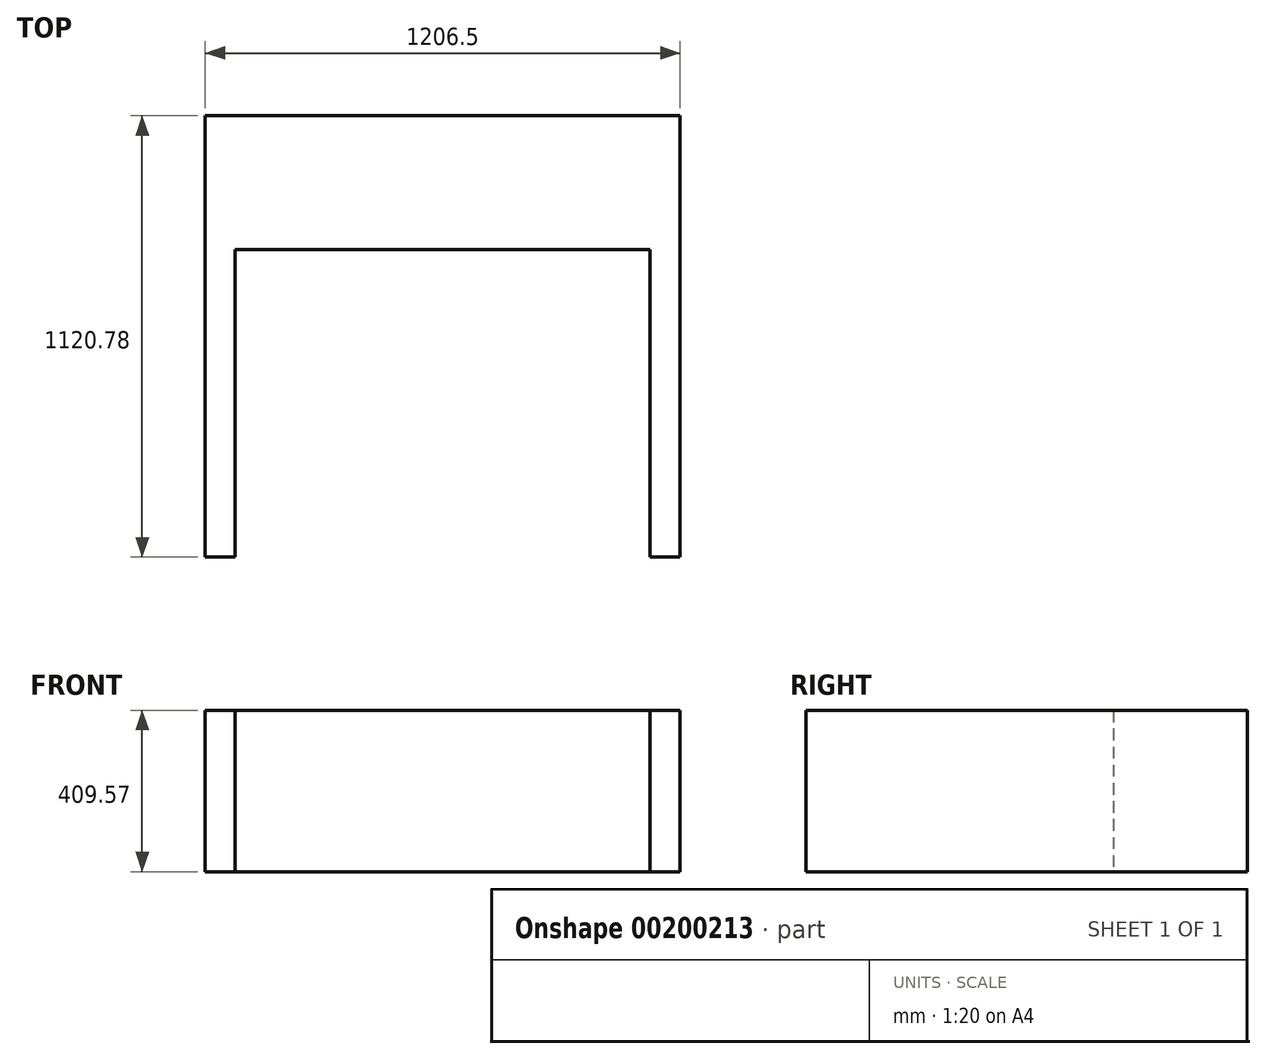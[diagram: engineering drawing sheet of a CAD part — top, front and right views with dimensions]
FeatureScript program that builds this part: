
annotation { "Feature Type Name" : "Feature", "Feature Type Description" : "" }
export const myFeature = defineFeature(function(context is Context, id is Id, definition is map)
    precondition{}
    {
        {
            var Q0;
            Q0=qCreatedBy(makeId("Front.planeOp"),FACE);
            var sketch = newSketch(context, id + "F0", { "sketchPlane" : qUnion([Q0])});
            skLineSegment(sketch, "E0.bottom", {"start": v(-1206.5, 308.58) * mm, "end": v(0, 308.58) * mm});
            skLineSegment(sketch, "E0.top", {"start": v(-1206.5, -101) * mm, "end": v(0, -101) * mm});
            skLineSegment(sketch, "E0.left", {"start": v(-1206.5, 308.58) * mm, "end": v(-1206.5, -101) * mm});
            skLineSegment(sketch, "E0.right", {"start": v(0, 308.58) * mm, "end": v(0, -101) * mm});
            skSolve(sketch);
        }
        {
            var Q0;
            Q0=makeQuery(id+"F0.imprint","IMPRINT",FACE,{"disambiguationData":[TD([[makeQuery(id+"F0.imprint","IMPRINT",EDGE,{"derivedFrom":sQuery(id+"F0.wireOp",EDGE,"E0.bottom")}),-1.0]])]});
            extrude(context, id + "F1", {"entities" : qUnion([Q0]), "depth" : 339.72 * mm});
        }
        {
            var Q0;
            Q0=makeQuery(id+"F1.opExtrude","CAP_FACE",FACE,{"disambiguationData":[OSD([sQuery(id+"F0.wireOp",EDGE,"E0.bottom"),sQuery(id+"F0.wireOp",EDGE,"E0.top"),sQuery(id+"F0.wireOp",EDGE,"E0.left"),sQuery(id+"F0.wireOp",EDGE,"E0.right")])],"isStart":false});
            var sketch = newSketch(context, id + "F2", { "sketchPlane" : qUnion([Q0])});
            skLineSegment(sketch, "E1.bottom", {"start": v(-1206.5, 308.58) * mm, "end": v(-1130.3, 308.58) * mm});
            skLineSegment(sketch, "E1.top", {"start": v(-1206.5, -101) * mm, "end": v(-1130.3, -101) * mm});
            skLineSegment(sketch, "E1.left", {"start": v(-1206.5, 308.58) * mm, "end": v(-1206.5, -101) * mm});
            skLineSegment(sketch, "E1.right", {"start": v(-1130.3, 308.58) * mm, "end": v(-1130.3, -101) * mm});
            skLineSegment(sketch, "E2.bottom", {"start": v(0, 308.58) * mm, "end": v(-76.2, 308.58) * mm});
            skLineSegment(sketch, "E2.top", {"start": v(0, -101) * mm, "end": v(-76.2, -101) * mm});
            skLineSegment(sketch, "E2.left", {"start": v(0, 308.58) * mm, "end": v(0, -101) * mm});
            skLineSegment(sketch, "E2.right", {"start": v(-76.2, 308.58) * mm, "end": v(-76.2, -101) * mm});
            skSolve(sketch);
        }
        {
            var Q0;
            Q0=makeQuery(id+"F2.imprint","IMPRINT",FACE,{"disambiguationData":[TD([[makeQuery(id+"F2.imprint","IMPRINT",EDGE,{"derivedFrom":sQuery(id+"F2.wireOp",EDGE,"E1.bottom")}),-1.0]])]});
            var Q1;
            Q1=makeQuery(id+"F2.imprint","IMPRINT",FACE,{"disambiguationData":[TD([[makeQuery(id+"F2.imprint","IMPRINT",EDGE,{"derivedFrom":sQuery(id+"F2.wireOp",EDGE,"E2.bottom")}),-1.0]])]});
            extrude(context, id + "F3", {"entities" : qUnion([Q0, Q1]), "operationType" : NewBodyOperationType.ADD, "depth" : 781.05 * mm});
        }
    });
